# Revit family: Faucet-Lavatory-KOHLER-PURIST-K-98423T_1
name_source: partatom
category: Plumbing Fixtures
revit_build: Autodesk Revit 2017 (Build: 20160225_1515(x64)
units: mm (PartAtom-declared; Revit-internal decimal feet)

## family parameters
Cut with Voids When Loaded = No
Host = Face
OmniClass Number = 23.31.11.00
Part Type = Normal
Room Calculation Point = No
Round Connector Dimension = Use Diameter
Shared = No

## types (4) — shared parameters
ADA Compliant = No
Assembly Code = D2010
CW Connection = Yes
Cold Water Inlet = Cold Water Inlet
Date Modified = 09/27/2020
Default Elevation = 36"
Drain Included = Yes
Flow Rate = 3 GPM
HW Connection = Yes
Handle Clearance = 2 13/16"
Height = 14 1/2"
Hot Water Inlet = Hot Water Inlet
Length = 6 1/4"
Manufacturer = KOHLER Co.
Master Format 2014 = 22 41 39
Master Format 2014 Name = Residential Faucets, Supplies, and Trim
Material = Premium Metal Construction
Pressure = 80.00 psi
Product Documentation Link = https://files.kohler.com.cn
Product Name = PURIST
Spout Reach = 6 1/4"
URL = http://www.kohler.com.cn
Vent Connection = No
Waste Connection = No
Waste Water Outlet = Waste Water Outlet
WaterSense Certified = No
Width = 2 1/4"

## per-type parameters (varying)
| type | Description | Finish | Model | Product Page URL | Sculpted Lever Handle | Straight Lever Handle | Type |
| Sculpted Lever Handle, CP-Polished Chrome | Single Handle Bowl Faucet (High Outlet)-Sculpted Lever Handle | Kohler-Metal-CP-Polished_Chrome | K-98423T-4-CP | https://www.kohler.com.cn | Yes | No | 1 |
| Sculpted Lever Handle, RGD-Rose Gold | Single Handle Bowl Faucet (High Outlet)-Sculpted Lever Handle | Kohler-Metal-RGD-Rose_Gold | K-98423T-4-RGD | https://www.kohler.com.cn | Yes | No | 2 |
| Straight Lever Handle, CP-Polished Chrome | Single Handle Bowl Faucet (High Outlet)-Straight Lever Handle | Kohler-Metal-CP-Polished_Chrome | K-98423T-4A-CP |  | No | Yes | 3 |
| Straight Lever Handle, RGD-Rose Gold | Single Handle Bowl Faucet (High Outlet)-Straight Lever Handle | Kohler-Metal-RGD-Rose_Gold | K-98423T-4A-RGD |  | No | Yes | 4 |

## geometry (parser evidence)
native form markers: Sweep x4
no freeform markers — native parametric forms only
